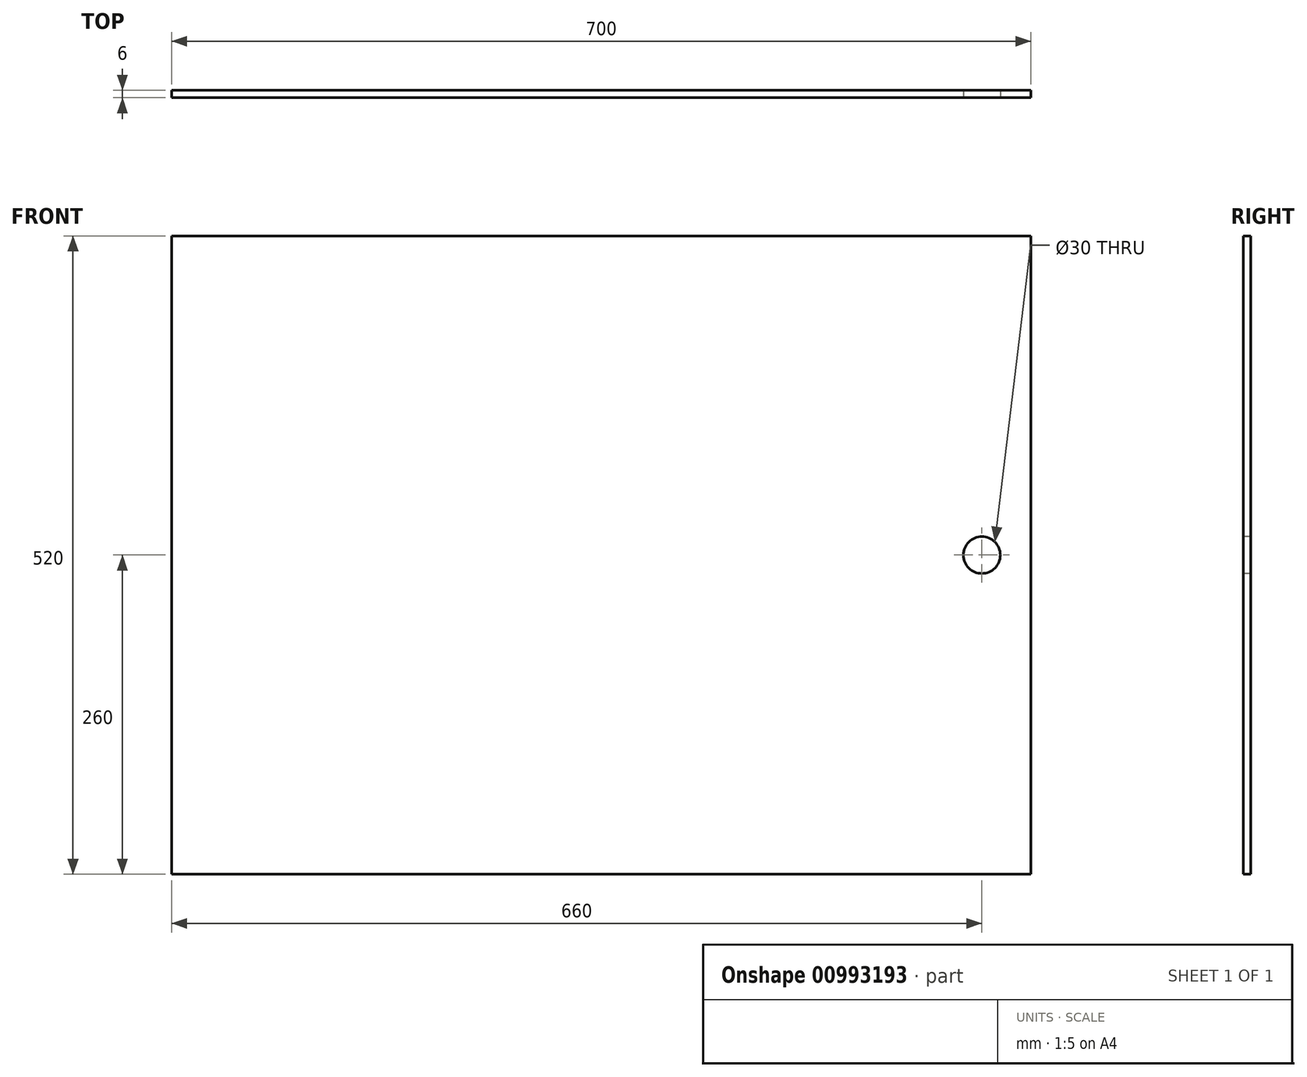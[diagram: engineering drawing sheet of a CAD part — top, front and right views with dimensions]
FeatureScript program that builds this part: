
annotation { "Feature Type Name" : "Feature", "Feature Type Description" : "" }
export const myFeature = defineFeature(function(context is Context, id is Id, definition is map)
    precondition{}
    {
        {
            var Q0;
            Q0=qCreatedBy(makeId("Front.planeOp"),FACE);
            var sketch = newSketch(context, id + "F0", { "sketchPlane" : qUnion([Q0])});
            skLineSegment(sketch, "E0.bottom", {"start": v(350, 260) * mm, "end": v(-350, 260) * mm});
            skLineSegment(sketch, "E0.top", {"start": v(350, -260) * mm, "end": v(-350, -260) * mm});
            skLineSegment(sketch, "E0.left", {"start": v(350, 260) * mm, "end": v(350, -260) * mm});
            skLineSegment(sketch, "E0.right", {"start": v(-350, 260) * mm, "end": v(-350, -260) * mm});
            skPoint(sketch, "E0.middle", {"position": v(0, 0) * mm});
            skCircle(sketch, "E1", {"center": v(310, 0) * mm, "radius": 15 * mm});
            skSolve(sketch);
        }
        {
            var Q0;
            Q0 = qSketchRegion(id + "F0", true);
            extrude(context, id + "F1", {"entities" : qUnion([Q0]), "oppositeDirection" : true, "depth" : 6 * mm, "offsetDistance" : 25 * mm});
        }
    });
